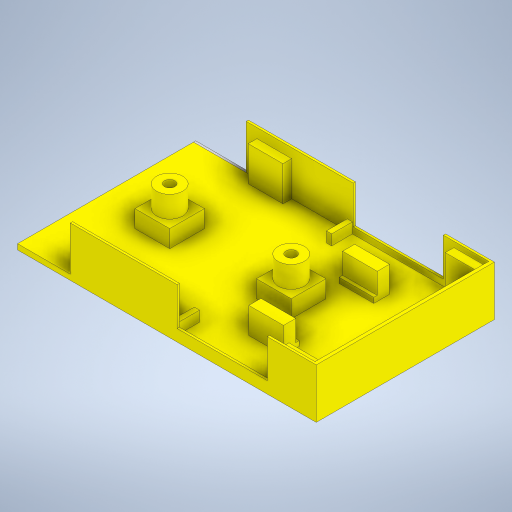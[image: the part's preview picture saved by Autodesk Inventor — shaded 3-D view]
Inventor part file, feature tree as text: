
AUTODESK INVENTOR PART (.ipt)
format: ipt  version: 2024 (Build 280153000, 153)  size: 878,592 bytes
history: native  units: mm
features: extrude x17, sketch x16, mirror x5
ambient origin geometry x8: Origin, YZ Plane, XZ Plane, XY Plane, X Axis, Y Axis, Z Axis, Center Point
bodies: Solid1 (feature_tree)
feature tree (38):
  extrude  "Extrusion1"  Depth=100.0mm
  sketch  "Sketch2"  dims[d2=3.125mm d3=0.0mm d4=20.0mm]
  extrude  "Extrusion2"  Depth=20.0mm
  extrude  "Extrusion3"  Depth=15.0mm
  extrude  "Extrusion4"  Depth=10.0mm TaperAngle=0.0deg
  extrude  "Extrusion5"  Depth=7.0mm TaperAngle=0.0deg
  extrude  "Extrusion6"  Depth=6.0mm
  extrude  "Extrusion7"  Depth=1.3mm
  extrude  "Extrusion8"  Depth=2.0mm
  extrude  "Extrusion9"  Depth=1.3mm TaperAngle=0.0deg
  extrude  "Extrusion10"  Depth=2.0mm TaperAngle=0.0deg
  extrude  "Extrusion11"  Depth=5.0mm
  mirror  "Mirror1"
  extrude  "Extrusion12"  Depth=5.0mm
  extrude  "Extrusion13"  Depth=22.4mm TaperAngle=0.0deg
  mirror  "Mirror2"
  extrude  "Extrusion14"  Depth=15.0mm TaperAngle=0.0deg
  mirror  "Mirror3"
  extrude  "Extrusion15"  Depth=20.0mm
  mirror  "Mirror4"
  extrude  "Extrusion16"  Depth=3.0mm TaperAngle=0.0deg
  mirror  "Mirror5"
  extrude  "Extrusion19"  Depth=3.0mm
  sketch  "Sketch1"  dims[d0=170.0mm d1=100.0mm]
  sketch  "Sketch3"  dims[d5=20.0mm d6=15.0mm]
  sketch  "Sketch4"  dims[d7=22.4mm d8=0.0mm d9=10.0mm d10=0.0mm]
  sketch  "Sketch5"  dims[d11=6.0mm d12=7.0mm d13=0.0mm]
  sketch  "Sketch6"  dims[d14=20.0mm d15=20.0mm d16=15.0mm d17=6.0mm]
  sketch  "Sketch7"  dims[d18=7.0mm d19=0.0mm d20=1.3mm]
  sketch  "Sketch8"  dims[d21=1.3mm d22=2.0mm]
  sketch  "Sketch9"  dims[d23=25.525mm d24=0.0mm d25=1.3mm d26=0.0mm]
  sketch  "Sketch10"  dims[d27=1.3mm d28=0.0mm d29=2.0mm d30=0.0mm]
  sketch  "Sketch11"  dims[d31=20.0mm d32=5.0mm]
  sketch  "Sketch12"  dims[d33=20.0mm d34=5.0mm]
  sketch  "Sketch13"  dims[d35=22.4mm d36=0.0mm d37=27.4mm d38=0.0mm]
  sketch  "Sketch14"  dims[d39=7.0mm d40=15.0mm d41=0.0mm]
  sketch  "Sketch15"  dims[d42=19.5mm d43=20.0mm]
  sketch  "Sketch17"  dims[d44=2.0mm d45=3.0mm d46=0.0mm d47=3.0mm d48=12.0mm d49=6.0mm d50=0.0mm d51=20.0mm d52=5.0mm d53=20.0mm d54=0.0mm d55=20.0mm d56=0.0mm d64=0.922mm d65=0.0mm]
